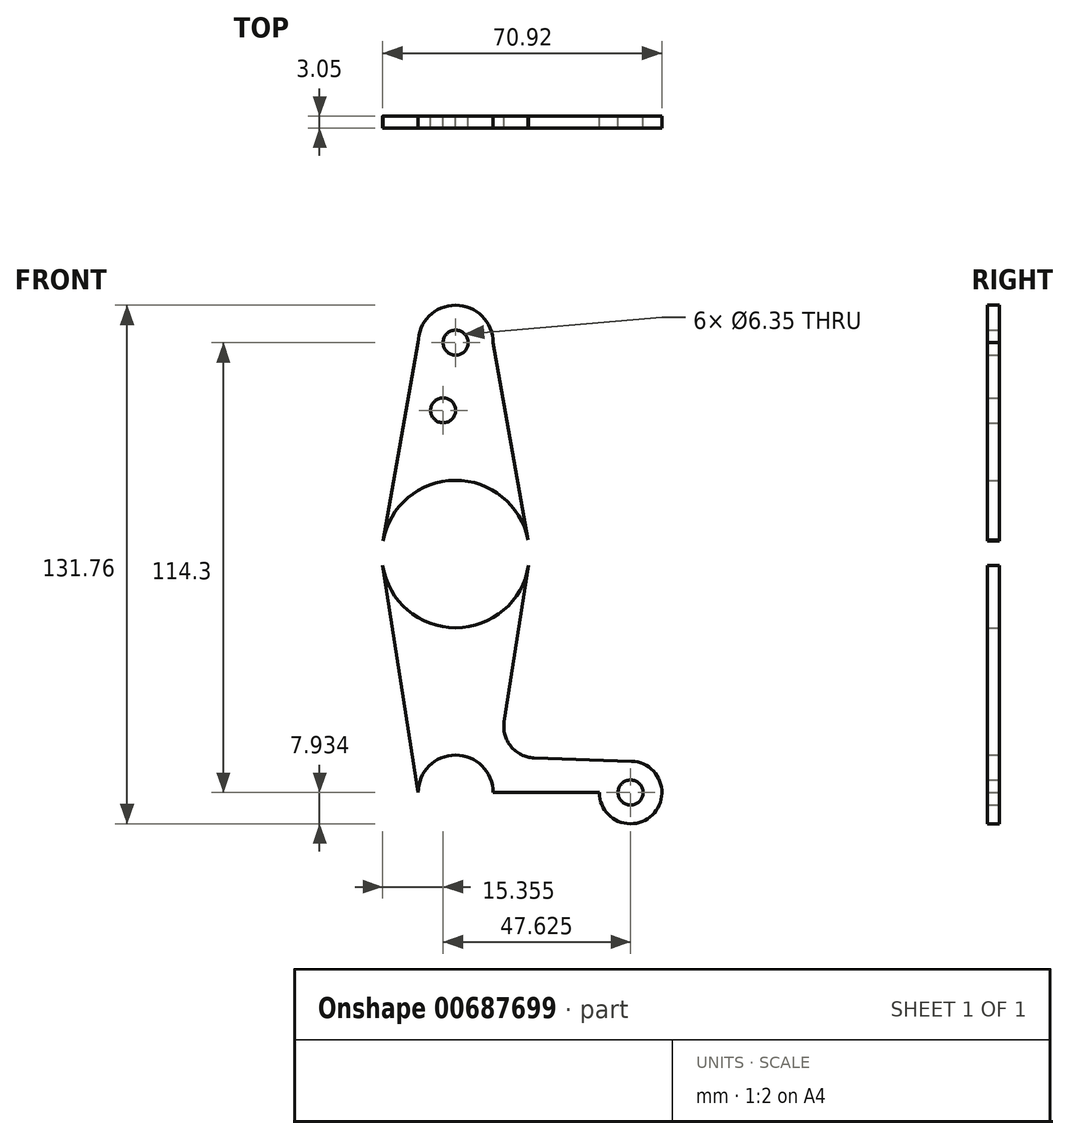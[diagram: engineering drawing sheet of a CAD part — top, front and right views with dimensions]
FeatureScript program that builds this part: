
annotation { "Feature Type Name" : "Feature", "Feature Type Description" : "" }
export const myFeature = defineFeature(function(context is Context, id is Id, definition is map)
    precondition{}
    {
        {
            var Q0;
            Q0=qCreatedBy(makeId("Front.planeOp"),FACE);
            var sketch = newSketch(context, id + "F0", { "sketchPlane" : qUnion([Q0])});
            skLineSegment(sketch, "E0", {"start": v(0, 53.71) * mm, "end": v(0, -60.59) * mm});
            skLineSegment(sketch, "E1", {"start": v(0, -60.59) * mm, "end": v(0, 2.91) * mm});
            skCircle(sketch, "E2", {"center": v(0, 53.71) * mm, "radius": 9.53 * mm});
            skCircle(sketch, "E3", {"center": v(0, 0) * mm, "radius": 18.75 * mm});
            skCircle(sketch, "E4", {"center": v(0, -60.59) * mm, "radius": 9.53 * mm});
            skLineSegment(sketch, "E5", {"start": v(0, -60.59) * mm, "end": v(44.45, -60.59) * mm});
            skCircle(sketch, "E6", {"center": v(44.45, -60.59) * mm, "radius": 7.94 * mm});
            skLineSegment(sketch, "E7", {"start": v(0, -70.11) * mm, "end": v(44.73, -68.52) * mm});
            skLineSegment(sketch, "E8", {"start": v(-9.53, 53.71) * mm, "end": v(-18.46, 3.27) * mm});
            skLineSegment(sketch, "E9", {"start": v(-9.52, -60.59) * mm, "end": v(-18.53, -2.9) * mm});
            skLineSegment(sketch, "E10", {"start": v(18.52, 2.91) * mm, "end": v(9.53, 53.71) * mm});
            skCircle(sketch, "E11", {"center": v(0, 53.71) * mm, "radius": 3.18 * mm});
            skCircle(sketch, "E12", {"center": v(0, 0) * mm, "radius": 3.18 * mm});
            skCircle(sketch, "E13", {"center": v(0, -60.59) * mm, "radius": 3.18 * mm});
            skCircle(sketch, "E14", {"center": v(44.45, -60.59) * mm, "radius": 3.18 * mm});
            skLineSegment(sketch, "E15", {"start": v(0, 0) * mm, "end": v(0, 36.53) * mm});
            skCircle(sketch, "E16", {"center": v(-3.17, 36.53) * mm, "radius": 3.17 * mm});
            skLineSegment(sketch, "E17", {"start": v(44.73, -52.65) * mm, "end": v(19.9, -51.77) * mm});
            skLineSegment(sketch, "E18", {"start": v(12.33, -42.6) * mm, "end": v(18.53, -2.9) * mm});
            skPoint(sketch, "E19.visualSharp", {"position": v(10.95, -51.45) * mm});
            skArc(sketch, "E19.filletArc", {"start": v(12.33, -42.6) * mm, "mid": v(14.06, -48.89) * mm, "end": v(19.9, -51.77) * mm});
            skSolve(sketch);
        }
        {
            var Q0;
            {var subQ10=sQuery(id+"F0.wireOp",EDGE,"E17");Q0=makeQuery(id+"F0.imprint","IMPRINT",FACE,{"disambiguationData":[TD([[makeQuery(id+"F0.imprint","IMPRINT",EDGE,{"derivedFrom":subQ10}),1.0]])]});}
            var Q1;
            {var subQ0=sQuery(id+"F0.wireOp",EDGE,"E7");var subQ1=sQuery(id+"F0.wireOp",EDGE,"E4");var subQ2=makeQuery(id+"F0.imprint","INTERSECT",VERTEX,{"disambiguationData":[OD(1.0)],"derivedFrom":[subQ1,subQ0]});Q1=makeQuery(id+"F0.imprint","IMPRINT",FACE,{"disambiguationData":[TD([[makeQuery(id+"F0.imprint","IMPRINT",EDGE,{"disambiguationData":[TD([[subQ2,-1.0]])],"derivedFrom":subQ1}),-1.0]])]});}
            var Q2;
            {var subQ0=sQuery(id+"F0.wireOp",EDGE,"E3");var subQ2=sQuery(id+"F0.wireOp",EDGE,"E1");var subQ3=makeQuery(id+"F0.imprint","INTERSECT",VERTEX,{"derivedFrom":[subQ2,subQ0]});Q2=makeQuery(id+"F0.imprint","IMPRINT",FACE,{"disambiguationData":[TD([[makeQuery(id+"F0.imprint","IMPRINT",EDGE,{"disambiguationData":[TD([[subQ3,-1.0]])],"derivedFrom":subQ2}),1.0]])]});}
            var Q3;
            {var subQ1=sQuery(id+"F0.wireOp",EDGE,"E3");var subQ4=sQuery(id+"F0.wireOp",EDGE,"E1");var subQ5=makeQuery(id+"F0.imprint","INTERSECT",VERTEX,{"derivedFrom":[subQ4,subQ1]});Q3=makeQuery(id+"F0.imprint","IMPRINT",FACE,{"disambiguationData":[TD([[makeQuery(id+"F0.imprint","IMPRINT",EDGE,{"disambiguationData":[TD([[subQ5,-1.0]])],"derivedFrom":subQ4}),-1.0]])]});}
            var Q4;
            {var subQ0=sQuery(id+"F0.wireOp",EDGE,"E13");var subQ1=sQuery(id+"F0.wireOp",EDGE,"E1");var subQ2=makeQuery(id+"F0.imprint","INTERSECT",VERTEX,{"derivedFrom":[subQ1,subQ0]});Q4=makeQuery(id+"F0.imprint","IMPRINT",FACE,{"disambiguationData":[TD([[makeQuery(id+"F0.imprint","IMPRINT",EDGE,{"disambiguationData":[TD([[subQ2,-1.0]])],"derivedFrom":subQ1}),-1.0]])]});}
            var Q5;
            {var subQ7=sQuery(id+"F0.wireOp",EDGE,"E1");var subQ9=sQuery(id+"F0.wireOp",EDGE,"E13");var subQ10=makeQuery(id+"F0.imprint","INTERSECT",VERTEX,{"derivedFrom":[subQ7,subQ9]});Q5=makeQuery(id+"F0.imprint","IMPRINT",FACE,{"disambiguationData":[TD([[makeQuery(id+"F0.imprint","IMPRINT",EDGE,{"disambiguationData":[TD([[subQ10,-1.0]])],"derivedFrom":subQ7}),1.0]])]});}
            var Q6;
            {var subQ0=sQuery(id+"F0.wireOp",EDGE,"E8");Q6=makeQuery(id+"F0.imprint","IMPRINT",FACE,{"disambiguationData":[TD([[makeQuery(id+"F0.imprint","IMPRINT",EDGE,{"derivedFrom":subQ0}),1.0]])]});}
            var Q7;
            {var subQ0=sQuery(id+"F0.wireOp",EDGE,"E10");var subQ1=sQuery(id+"F0.wireOp",EDGE,"E2");var subQ2=makeQuery(id+"F0.imprint","INTERSECT",VERTEX,{"derivedFrom":[subQ1,subQ0]});Q7=makeQuery(id+"F0.imprint","IMPRINT",FACE,{"disambiguationData":[TD([[makeQuery(id+"F0.imprint","IMPRINT",EDGE,{"disambiguationData":[TD([[subQ2,1.0]])],"derivedFrom":subQ1}),-1.0]])]});}
            var Q8;
            {var subQ5=sQuery(id+"F0.wireOp",EDGE,"E9");Q8=makeQuery(id+"F0.imprint","IMPRINT",FACE,{"disambiguationData":[TD([[makeQuery(id+"F0.imprint","IMPRINT",EDGE,{"derivedFrom":subQ5}),-1.0]])]});}
            var Q9;
            Q9=makeQuery(id+"F0.imprint","IMPRINT",FACE,{"disambiguationData":[TD([[makeQuery(id+"F0.imprint","IMPRINT",EDGE,{"derivedFrom":sQuery(id+"F0.wireOp",EDGE,"E14")}),-1.0]])]});
            var Q10;
            Q10=makeQuery(id+"F0.imprint","IMPRINT",FACE,{"disambiguationData":[TD([[makeQuery(id+"F0.imprint","IMPRINT",EDGE,{"derivedFrom":sQuery(id+"F0.wireOp",EDGE,"E11")}),-1.0]])]});
            extrude(context, id + "F1", {"entities" : qUnion([Q0, Q1, Q2, Q3, Q4, Q5, Q6, Q7, Q8, Q9, Q10]), "depth" : 3.05 * mm, "offsetDistance" : 25.4 * mm});
        }
    });
